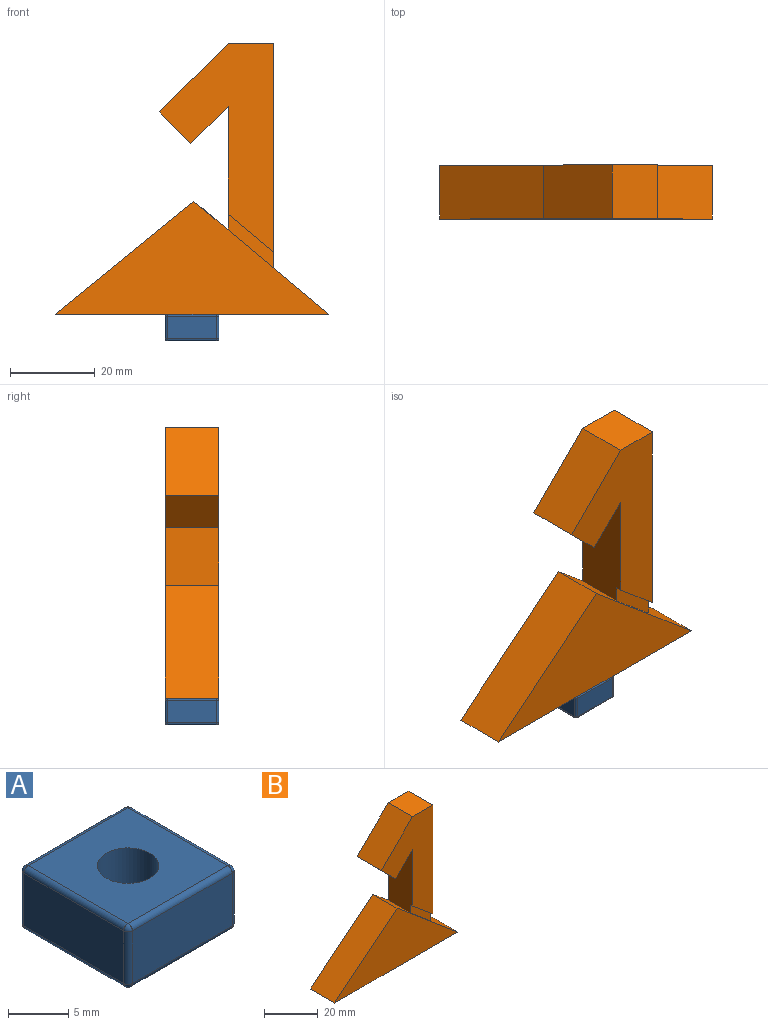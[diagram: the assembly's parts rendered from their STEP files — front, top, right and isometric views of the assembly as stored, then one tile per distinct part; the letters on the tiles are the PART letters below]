
ASSEMBLY  parts=2 mates=1
PART A: 28 faces, bbox 12.7x12.7x6.4 mm
  f0: plane 11.68x5.33mm, normal (0,-1,0), area 62.3mm2, adj f16,f21,f24,f27
  f1: plane 11.68x5.33mm, normal (1,0,0), area 62.3mm2, adj f13,f22,f23,f27
  f2: plane 11.68x5.33mm, normal (0,1,0), area 62.3mm2, adj f8,f12,f13,f14
  f3: cylinder r=2.54mm len=5.08mm, axis (0,0,-1), area 60.8mm2, adj f5,f7
  f4: plane 11.68x5.33mm, normal (-1,0,0), area 62.3mm2, adj f8,f11,f15,f16
  f5: plane 11.68x11.68mm, normal (0,0,1), area 116.2mm2, adj f3,f11,f12,f21,f22
  f6: plane 11.68x11.68mm, normal (0,0,-1), area 55.4mm2, adj f7,f14,f15,f23,f24
  f7: cone r=5.08mm half-angle=45deg, axis (0,0,-1), area 86mm2, adj f3,f6
  f8: cylinder r=0.51mm len=5.33mm, axis (0,0,-1), area 4.3mm2, adj f2,f4,f9,f10
  f9: sphere r=0.51mm, area 0.4mm2, adj f8,f11,f12
  f10: sphere r=0.51mm, area 0.4mm2, adj f8,f14,f15
  f11: cylinder r=0.51mm len=11.68mm, axis (0,1,0), area 9.3mm2, adj f4,f5,f9,f17
  f12: cylinder r=0.51mm len=11.68mm, axis (1,0,0), area 9.3mm2, adj f2,f5,f9,f18
  f13: cylinder r=0.51mm len=5.33mm, axis (0,0,1), area 4.3mm2, adj f1,f2,f18,f19
  f14: cylinder r=0.51mm len=11.68mm, axis (-1,0,0), area 9.3mm2, adj f2,f6,f10,f19
  f15: cylinder r=0.51mm len=11.68mm, axis (0,-1,0), area 9.3mm2, adj f4,f6,f10,f20
  f16: cylinder r=0.51mm len=5.33mm, axis (0,0,1), area 4.3mm2, adj f0,f4,f17,f20
  f17: sphere r=0.51mm, area 0.4mm2, adj f11,f16,f21
  f18: sphere r=0.51mm, area 0.4mm2, adj f12,f13,f22
  f19: sphere r=0.51mm, area 0.4mm2, adj f13,f14,f23
  f20: sphere r=0.51mm, area 0.4mm2, adj f15,f16,f24
  f21: cylinder r=0.51mm len=11.68mm, axis (-1,0,0), area 9.3mm2, adj f0,f5,f17,f25
  f22: cylinder r=0.51mm len=11.68mm, axis (0,-1,0), area 9.3mm2, adj f1,f5,f18,f25
  f23: cylinder r=0.51mm len=11.68mm, axis (0,1,0), area 9.3mm2, adj f1,f6,f19,f26
  f24: cylinder r=0.51mm len=11.68mm, axis (1,0,0), area 9.3mm2, adj f0,f6,f20,f26
  f25: sphere r=0.51mm, area 0.4mm2, adj f21,f22,f27
  f26: sphere r=0.51mm, area 0.4mm2, adj f23,f24,f27
  f27: cylinder r=0.51mm len=5.33mm, axis (0,0,-1), area 4.3mm2, adj f0,f1,f25,f26
PART B: 14 faces, bbox 64.5x12.7x64.2 mm
  f0: plane 31.76x26.69mm, normal (0.64,0,0.77), area 367.8mm2, adj f1,f2,f3,f4,f5,f8,f13
  f1: plane 32.7x26.69mm, normal (-0.63,0,0.77), area 536mm2, adj f0,f2,f3,f4
  f2: plane 64.46x12.7mm, normal (0,0,-1), area 818.6mm2, adj f0,f1,f3,f4
  f3: plane 64.46x26.69mm, normal (0,-1,0), area 860.3mm2, adj f0,f1,f2
  f4: plane 64.46x64.17mm, normal (0,1,0), area 1568.9mm2, adj f0,f1,f2,f5,f6,f7,f8,f9
  f5: plane 53.23x12.7mm, normal (1,0,0), area 671.2mm2, adj f0,f4,f6,f11,f12,f13
  f6: plane 12.7x10.66mm, normal (0,0,1), area 135.4mm2, adj f4,f5,f7,f12
  f7: plane 16.33x16.32mm, normal (-0.71,0,0.71), area 293.2mm2, adj f4,f6,f9,f12
  f8: plane 29.25x12.7mm, normal (-1,0,0), area 366.7mm2, adj f0,f4,f10,f11,f12,f13
  f9: plane 12.7x7.52mm, normal (-0.71,0,-0.71), area 135mm2, adj f4,f7,f10,f12
  f10: plane 12.7x8.82mm, normal (0.71,0,-0.71), area 158.3mm2, adj f4,f8,f9,f12
  f11: plane 10.66x8.96mm, normal (-0.64,0,-0.77), area 17.7mm2, adj f5,f8,f12,f13
  f12: plane 49.48x26.99mm, normal (0,-1,0), area 668.7mm2, adj f5,f6,f7,f8,f9,f10,f11
  f13: plane 12.7x10.66mm, normal (0,-1,0), area 39.9mm2, adj f0,f5,f8,f11
PLACE A t=(-6.6,2.12,-0.46)mm
PLACE B t=(-6.14,2.12,32.58)mm
MATE revolute B.f2 <-> A.f3  axis (0,0,-1) through (-6.6,2.12,5.89)mm
